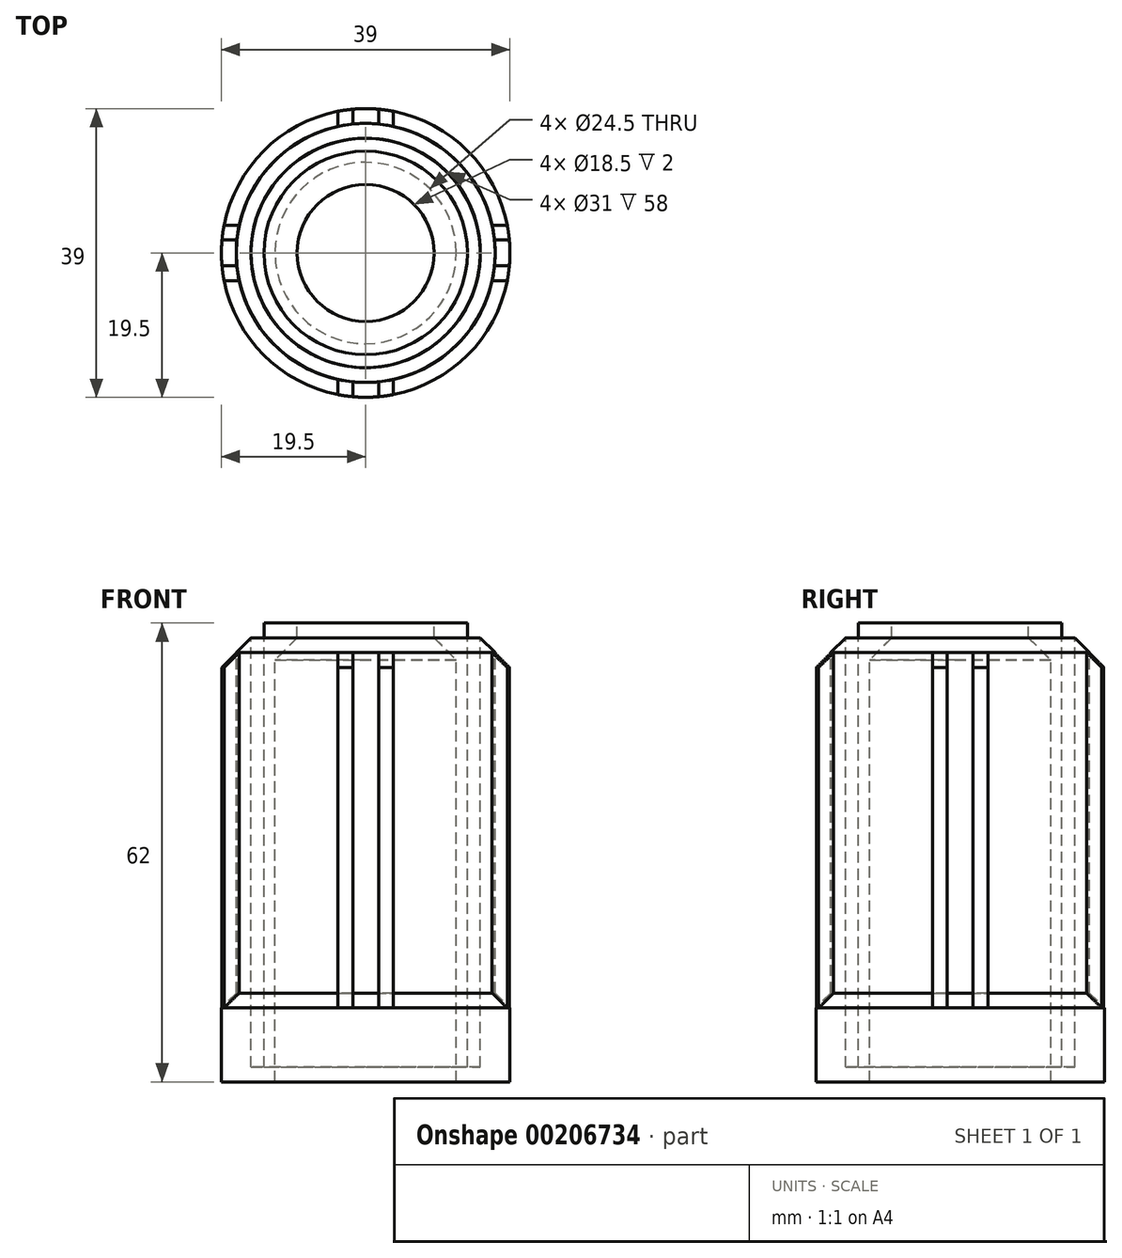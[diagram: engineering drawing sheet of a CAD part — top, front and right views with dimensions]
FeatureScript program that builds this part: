
annotation { "Feature Type Name" : "Feature", "Feature Type Description" : "" }
export const myFeature = defineFeature(function(context is Context, id is Id, definition is map)
    precondition{}
    {
        {
            var Q0;
            Q0=qCreatedBy(makeId("Right.planeOp"),FACE);
            var sketch = newSketch(context, id + "F0", { "sketchPlane" : qUnion([Q0])});
            skLineSegment(sketch, "E0", {"start": v(-9.25, 2) * mm, "end": v(-13.75, 2) * mm});
            skLineSegment(sketch, "E1", {"start": v(-13.75, 2) * mm, "end": v(-13.75, -58) * mm});
            skLineSegment(sketch, "E2", {"start": v(-13.75, -58) * mm, "end": v(-15.5, -58) * mm});
            skLineSegment(sketch, "E3", {"start": v(-15.5, -58) * mm, "end": v(-15.5, 0) * mm});
            skLineSegment(sketch, "E4", {"start": v(-15.5, 0) * mm, "end": v(-17.5, 0) * mm});
            skLineSegment(sketch, "E5", {"start": v(-17.5, 0) * mm, "end": v(-17.5, -50) * mm});
            skLineSegment(sketch, "E6", {"start": v(-17.5, -60) * mm, "end": v(-12.25, -60) * mm});
            skLineSegment(sketch, "E7", {"start": v(-12.25, -60) * mm, "end": v(-12.25, 0) * mm});
            skLineSegment(sketch, "E8", {"start": v(-12.25, 0) * mm, "end": v(-9.25, 0) * mm});
            skLineSegment(sketch, "E9", {"start": v(-9.25, 2) * mm, "end": v(-9.25, 0) * mm});
            skPoint(sketch, "E10.orphan", {"position": v(-9.25, -22.62) * mm});
            skPoint(sketch, "E11.orphan", {"position": v(-9.25, 0) * mm});
            skLineSegment(sketch, "E12", {"start": v(-17.5, -60) * mm, "end": v(-19.5, -60) * mm});
            skLineSegment(sketch, "E13", {"start": v(-19.5, -60) * mm, "end": v(-19.5, -50) * mm});
            skLineSegment(sketch, "E14", {"start": v(-19.5, -50) * mm, "end": v(-17.5, -50) * mm});
            skLineSegment(sketch, "E15", {"start": v(-9.25, 0) * mm, "end": v(-12.25, -3) * mm});
            skSolve(sketch);
        }
        {
            var Q0;
            Q0=qCreatedBy(makeId("Right.planeOp"),FACE);
            var sketch = newSketch(context, id + "F1", { "sketchPlane" : qUnion([Q0])});
            skLineSegment(sketch, "E16", {"start": v(0, 50.87) * mm, "end": v(0, -29.55) * mm, "construction": true});
            skSolve(sketch);
        }
        {
            var Q0;
            Q0 = qSketchRegion(id + "F0", true);
            var Q1;
            Q1=sQuery(id+"F1.wireOp",EDGE,"E16");
            revolve(context, id + "F2", {"entities" : qUnion([Q0]), "axis" : qUnion([Q1]), "revolveType" : RevolveType.FULL});
        }
        {
            var Q0;
            Q0=makeQuery(id+"F2.opRevolve","SWEPT_FACE",FACE,{"disambiguationData":[OSD([sQuery(id+"F0.wireOp",EDGE,"E5")])]});
            chamfer(context, id + "F3", {"entities" : qUnion([Q0]), "width" : 2 * mm, "tangentPropagation" : true});
        }
        {
            var Q0;
            Q0=makeQuery(id+"F2.opRevolve","SWEPT_FACE",FACE,{"disambiguationData":[OSD([sQuery(id+"F0.wireOp",EDGE,"E6"),sQuery(id+"F0.wireOp",EDGE,"E12")])]});
            cPlane(context, id + "F4", {"entities" : qUnion([Q0]), "cplaneType" : CPlaneType.OFFSET, "offset" : 0 * mm, "width" : 150 * mm, "height" : 150 * mm});
        }
        {
            var Q0;
            Q0=qCreatedBy(id+"F4.planeOp",FACE);
            var sketch = newSketch(context, id + "F5", { "sketchPlane" : qUnion([Q0])});
            skLineSegment(sketch, "E17", {"start": v(0, 0) * mm, "end": v(-19.5, 0) * mm, "construction": true});
            skLineSegment(sketch, "E18.bottom", {"start": v(-16.5, 1.75) * mm, "end": v(-19.5, 1.75) * mm});
            skLineSegment(sketch, "E18.top", {"start": v(-16.5, 3.75) * mm, "end": v(-19.5, 3.75) * mm});
            skLineSegment(sketch, "E18.left", {"start": v(-16.5, 1.75) * mm, "end": v(-16.5, 3.75) * mm});
            skLineSegment(sketch, "E18.right", {"start": v(-19.5, 1.75) * mm, "end": v(-19.5, 3.75) * mm});
            skCircle(sketch, "E19.0", {"center": v(0, 0) * mm, "radius": 19.5 * mm});
            skLineSegment(sketch, "E20.MirrorCS", {"start": v(-16.5, -1.75) * mm, "end": v(-19.5, -1.75) * mm});
            skLineSegment(sketch, "E21.MirrorCS", {"start": v(-16.5, -1.75) * mm, "end": v(-16.5, -3.75) * mm});
            skLineSegment(sketch, "E22.MirrorCS", {"start": v(-19.5, -1.75) * mm, "end": v(-19.5, -3.75) * mm});
            skLineSegment(sketch, "E23.MirrorCS", {"start": v(-16.5, -3.75) * mm, "end": v(-19.5, -3.75) * mm});
            skSolve(sketch);
        }
        {
            var Q0;
            {var subQ0=sQuery(id+"F5.wireOp",EDGE,"E18.left");Q0=makeQuery(id+"F5.imprint","IMPRINT",FACE,{"disambiguationData":[TD([[makeQuery(id+"F5.imprint","IMPRINT",EDGE,{"derivedFrom":subQ0}),1.0]])]});}
            var Q1;
            {var subQ5=sQuery(id+"F5.wireOp",EDGE,"E21.MirrorCS");Q1=makeQuery(id+"F5.imprint","IMPRINT",FACE,{"disambiguationData":[TD([[makeQuery(id+"F5.imprint","IMPRINT",EDGE,{"derivedFrom":subQ5}),-1.0]])]});}
            extrude(context, id + "F6", {"entities" : qUnion([Q0, Q1]), "operationType" : NewBodyOperationType.ADD, "oppositeDirection" : true, "depth" : 58 * mm});
        }
        {
            var Q0;
            {var subQ0=sQuery(id+"F5.wireOp",EDGE,"E19.0");Q0=makeQuery(id+"F6.opExtrude","CAP_EDGE",EDGE,{"disambiguationData":[OSD([subQ0]),TDD([makeQuery(id+"F5.imprint","IMPRINT",EDGE,{"disambiguationData":[TD([[makeQuery(id+"F5.imprint","INTERSECT",VERTEX,{"derivedFrom":[sQuery(id+"F5.wireOp",EDGE,"E18.bottom"),subQ0]}),1.0]])],"derivedFrom":subQ0})])],"isStart":false});}
            var Q1;
            {var subQ0=sQuery(id+"F5.wireOp",EDGE,"E19.0");Q1=makeQuery(id+"F6.opExtrude","CAP_EDGE",EDGE,{"disambiguationData":[OSD([subQ0]),TDD([makeQuery(id+"F5.imprint","IMPRINT",EDGE,{"disambiguationData":[TD([[makeQuery(id+"F5.imprint","INTERSECT",VERTEX,{"derivedFrom":[subQ0,sQuery(id+"F5.wireOp",EDGE,"E20.MirrorCS")]}),-1.0]])],"derivedFrom":subQ0})])],"isStart":false});}
            chamfer(context, id + "F7", {"entities" : qUnion([Q0, Q1]), "width" : 2 * mm, "tangentPropagation" : true});
        }
        {
            var Q0;
            Q0=makeQuery(id+"F2.opRevolve","SWEPT_BODY",BODY,{"disambiguationData":[OSD([sQuery(id+"F0.wireOp",EDGE,"E0"),sQuery(id+"F0.wireOp",EDGE,"E1"),sQuery(id+"F0.wireOp",EDGE,"E2"),sQuery(id+"F0.wireOp",EDGE,"E3"),sQuery(id+"F0.wireOp",EDGE,"E4"),sQuery(id+"F0.wireOp",EDGE,"E5"),sQuery(id+"F0.wireOp",EDGE,"E6"),sQuery(id+"F0.wireOp",EDGE,"E7"),sQuery(id+"F0.wireOp",EDGE,"E8"),sQuery(id+"F0.wireOp",EDGE,"E9"),sQuery(id+"F0.wireOp",EDGE,"E12"),sQuery(id+"F0.wireOp",EDGE,"E13"),sQuery(id+"F0.wireOp",EDGE,"E14")])]});
            var Q1;
            Q1=sQuery(id+"F1.wireOp",EDGE,"E16");
            circularPattern(context, id + "F8", {"entities" : qUnion([Q0]), "axis" : qUnion([Q1]), "angle" : 360 * degree, "instanceCount" : 4, "equalSpace" : true});
        }
    });
